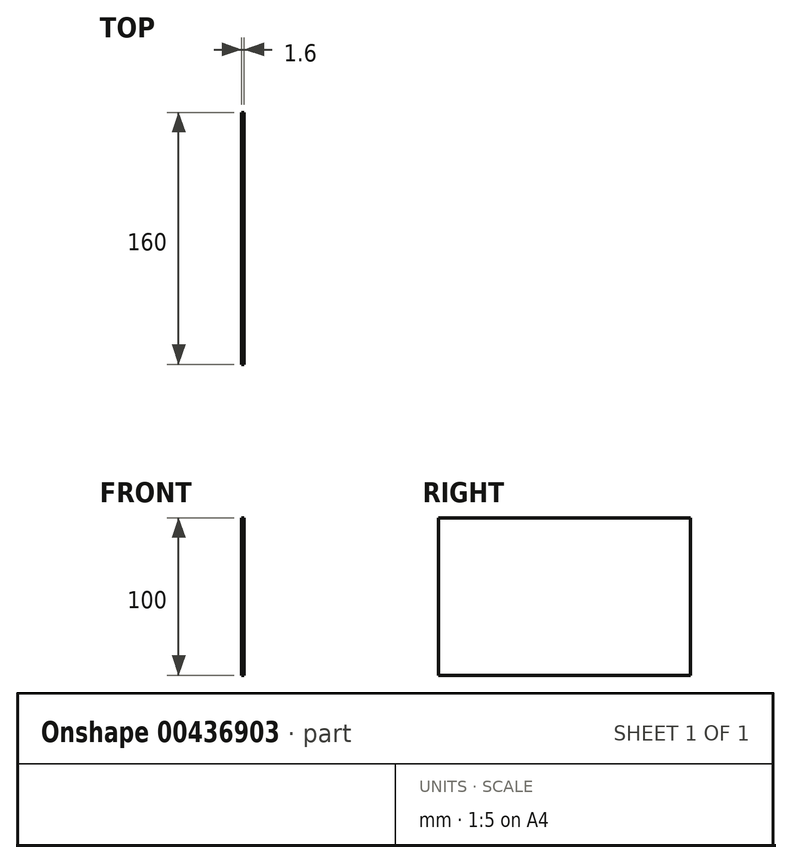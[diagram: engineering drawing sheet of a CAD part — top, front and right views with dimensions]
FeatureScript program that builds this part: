
annotation { "Feature Type Name" : "Feature", "Feature Type Description" : "" }
export const myFeature = defineFeature(function(context is Context, id is Id, definition is map)
    precondition{}
    {
        {
            var Q0;
            Q0=qCreatedBy(makeId("Right.planeOp"),FACE);
            var sketch = newSketch(context, id + "F0", { "sketchPlane" : qUnion([Q0])});
            skLineSegment(sketch, "E0.bottom", {"start": v(0, 0) * mm, "end": v(160, 0) * mm});
            skLineSegment(sketch, "E0.top", {"start": v(0, 100) * mm, "end": v(160, 100) * mm});
            skLineSegment(sketch, "E0.left", {"start": v(0, 0) * mm, "end": v(0, 100) * mm});
            skLineSegment(sketch, "E0.right", {"start": v(160, 0) * mm, "end": v(160, 100) * mm});
            skSolve(sketch);
        }
        {
            var Q0;
            Q0 = qSketchRegion(id + "F0", true);
            extrude(context, id + "F1", {"entities" : qUnion([Q0]), "depth" : 1.6 * mm});
        }
    });
